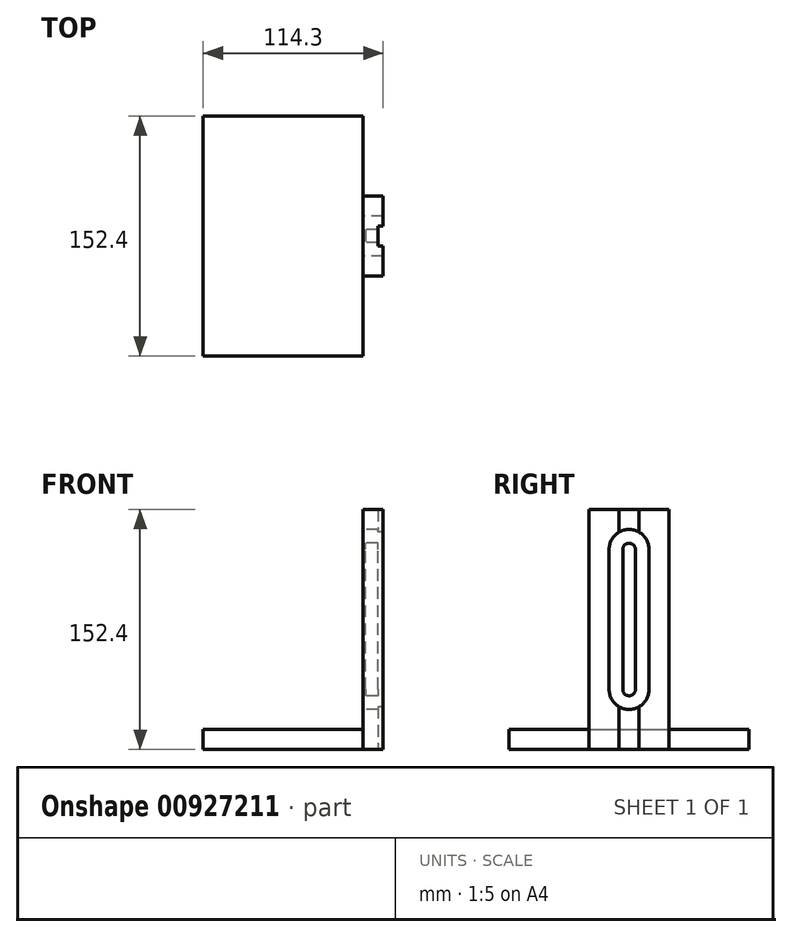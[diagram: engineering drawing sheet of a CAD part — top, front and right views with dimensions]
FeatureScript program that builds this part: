
annotation { "Feature Type Name" : "Feature", "Feature Type Description" : "" }
export const myFeature = defineFeature(function(context is Context, id is Id, definition is map)
    precondition{}
    {
        {
            var Q0;
            Q0=qCreatedBy(makeId("Front.planeOp"),FACE);
            var sketch = newSketch(context, id + "F0", { "sketchPlane" : qUnion([Q0])});
            skLineSegment(sketch, "E0.bottom", {"start": v(0, 0) * mm, "end": v(-12.7, 0) * mm});
            skLineSegment(sketch, "E0.top", {"start": v(0, 152.4) * mm, "end": v(-12.7, 152.4) * mm});
            skLineSegment(sketch, "E0.left", {"start": v(0, 0) * mm, "end": v(0, 152.4) * mm});
            skLineSegment(sketch, "E0.right", {"start": v(-12.7, 0) * mm, "end": v(-12.7, 152.4) * mm});
            skLineSegment(sketch, "E1.bottom", {"start": v(-12.7, 0) * mm, "end": v(-114.3, 0) * mm});
            skLineSegment(sketch, "E1.top", {"start": v(-12.7, 12.7) * mm, "end": v(-114.3, 12.7) * mm});
            skLineSegment(sketch, "E1.left", {"start": v(-12.7, 0) * mm, "end": v(-12.7, 12.7) * mm});
            skLineSegment(sketch, "E1.right", {"start": v(-114.3, 0) * mm, "end": v(-114.3, 12.7) * mm});
            skSolve(sketch);
        }
        {
            var Q0;
            Q0=makeQuery(id+"F0.imprint","IMPRINT",FACE,{"disambiguationData":[TD([[makeQuery(id+"F0.imprint","IMPRINT",EDGE,{"derivedFrom":sQuery(id+"F0.wireOp",EDGE,"E0.bottom")}),-1.0]])]});
            extrude(context, id + "F1", {"entities" : qUnion([Q0]), "endBound" : BoundingType.SYMMETRIC, "depth" : 50.8 * mm, "offsetDistance" : 25.4 * mm});
        }
        {
            var Q0;
            Q0=makeQuery(id+"F0.imprint","IMPRINT",FACE,{"disambiguationData":[TD([[makeQuery(id+"F0.imprint","IMPRINT",EDGE,{"derivedFrom":sQuery(id+"F0.wireOp",EDGE,"E1.bottom")}),-1.0]])]});
            extrude(context, id + "F2", {"entities" : qUnion([Q0]), "operationType" : NewBodyOperationType.ADD, "endBound" : BoundingType.SYMMETRIC, "depth" : 152.4 * mm, "offsetDistance" : 25.4 * mm});
        }
        {
            var Q0;
            Q0=makeQuery(id+"F2.boolean.opBoolean","MERGE",FACE,{"derivedFrom":[makeQuery(id+"F1.opExtrude","SWEPT_FACE",FACE,{"disambiguationData":[OSD([sQuery(id+"F0.wireOp",EDGE,"E0.bottom")])]}),makeQuery(id+"F2.opExtrude","SWEPT_FACE",FACE,{"disambiguationData":[OSD([sQuery(id+"F0.wireOp",EDGE,"E1.bottom")])]})]});
            var sketch = newSketch(context, id + "F3", { "sketchPlane" : qUnion([Q0])});
            skLineSegment(sketch, "E2.bottom", {"start": v(0, 6.35) * mm, "end": v(-3.18, 6.35) * mm});
            skLineSegment(sketch, "E2.top", {"start": v(0, -6.35) * mm, "end": v(-3.18, -6.35) * mm});
            skLineSegment(sketch, "E2.left", {"start": v(0, 6.35) * mm, "end": v(0, -6.35) * mm});
            skLineSegment(sketch, "E2.right", {"start": v(-3.18, 6.35) * mm, "end": v(-3.18, -6.35) * mm});
            skSolve(sketch);
        }
        {
            var Q0;
            Q0 = qSketchRegion(id + "F3", true);
            extrude(context, id + "F4", {"entities" : qUnion([Q0]), "operationType" : NewBodyOperationType.REMOVE, "endBound" : BoundingType.UP_TO_NEXT, "oppositeDirection" : true, "depth" : 25.4 * mm, "offsetDistance" : 25.4 * mm});
        }
        {
            var Q0;
            Q0=makeQuery(id+"F1.opExtrude","SWEPT_FACE",FACE,{"disambiguationData":[OSD([sQuery(id+"F0.wireOp",EDGE,"E0.right"),sQuery(id+"F0.wireOp",EDGE,"E1.left")])]});
            var sketch = newSketch(context, id + "F5", { "sketchPlane" : qUnion([Q0])});
            skLineSegment(sketch, "E3", {"start": v(0, 38.1) * mm, "end": v(0, 127) * mm, "construction": true});
            skArc(sketch, "E4.0.startCap", {"start": v(4, 38.1) * mm, "mid": v(0, 34.1) * mm, "end": v(-4, 38.1) * mm});
            skArc(sketch, "E4.0.endCap", {"start": v(-4, 127) * mm, "mid": v(0, 131) * mm, "end": v(4, 127) * mm});
            skLineSegment(sketch, "E4.0.left", {"start": v(-4, 38.1) * mm, "end": v(-4, 127) * mm});
            skLineSegment(sketch, "E4.0.right", {"start": v(4, 38.1) * mm, "end": v(4, 127) * mm});
            skArc(sketch, "E5.0.startCap", {"start": v(12.7, 38.1) * mm, "mid": v(0, 25.4) * mm, "end": v(-12.7, 38.1) * mm});
            skArc(sketch, "E5.0.endCap", {"start": v(-12.7, 127) * mm, "mid": v(0, 139.7) * mm, "end": v(12.7, 127) * mm});
            skLineSegment(sketch, "E5.0.left", {"start": v(-12.7, 38.1) * mm, "end": v(-12.7, 127) * mm});
            skLineSegment(sketch, "E5.0.right", {"start": v(12.7, 38.1) * mm, "end": v(12.7, 127) * mm});
            skSolve(sketch);
        }
        {
            var Q0;
            Q0=makeQuery(id+"F5.imprint","IMPRINT",FACE,{"disambiguationData":[TD([[makeQuery(id+"F5.imprint","IMPRINT",EDGE,{"derivedFrom":sQuery(id+"F5.wireOp",EDGE,"E4.0.startCap")}),-1.0]])]});
            extrude(context, id + "F6", {"entities" : qUnion([Q0]), "operationType" : NewBodyOperationType.REMOVE, "endBound" : BoundingType.THROUGH_ALL, "oppositeDirection" : true, "depth" : 25.4 * mm, "offsetDistance" : 25.4 * mm});
        }
        {
            var Q0;
            Q0=makeQuery(id+"F5.imprint","IMPRINT",FACE,{"disambiguationData":[TD([[makeQuery(id+"F5.imprint","IMPRINT",EDGE,{"derivedFrom":sQuery(id+"F5.wireOp",EDGE,"E4.0.startCap")}),1.0]])]});
            extrude(context, id + "F7", {"entities" : qUnion([Q0]), "operationType" : NewBodyOperationType.REMOVE, "oppositeDirection" : true, "depth" : 1.59 * mm, "offsetDistance" : 25.4 * mm});
        }
    });
